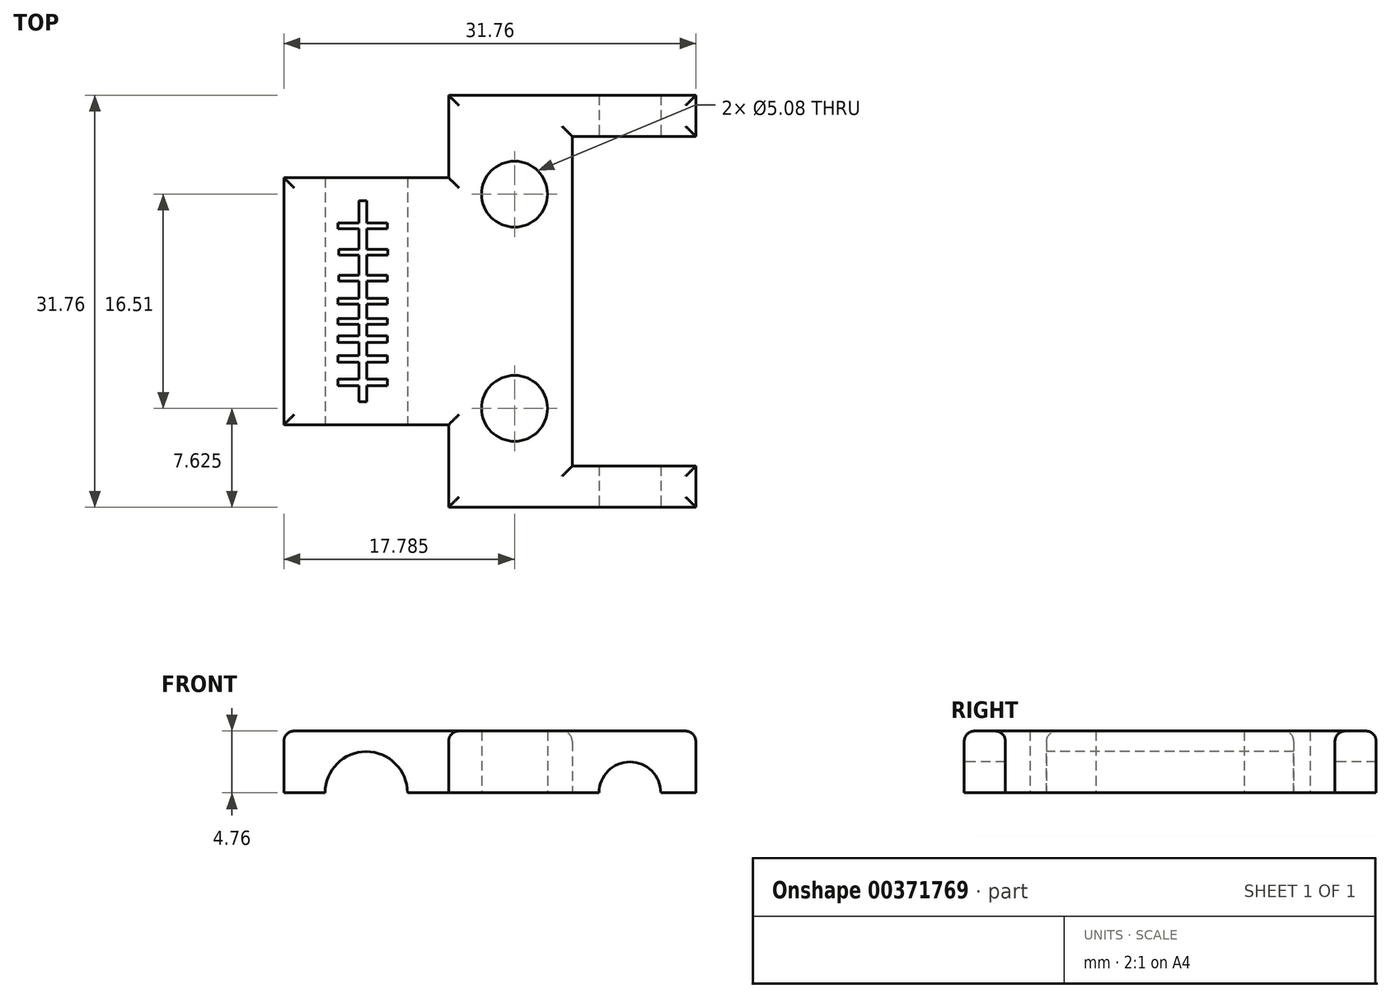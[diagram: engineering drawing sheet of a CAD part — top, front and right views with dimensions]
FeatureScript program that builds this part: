
annotation { "Feature Type Name" : "Feature", "Feature Type Description" : "" }
export const myFeature = defineFeature(function(context is Context, id is Id, definition is map)
    precondition{}
    {
        {
            var Q0;
            Q0=qCreatedBy(makeId("Top.planeOp"),FACE);
            var sketch = newSketch(context, id + "F0", { "sketchPlane" : qUnion([Q0])});
            skLineSegment(sketch, "E0.bottom", {"start": v(15.87, 15.87) * mm, "end": v(-3.18, 15.87) * mm});
            skLineSegment(sketch, "E0.top", {"start": v(15.88, -15.87) * mm, "end": v(-3.17, -15.87) * mm});
            skLineSegment(sketch, "E0.left", {"start": v(15.87, 15.88) * mm, "end": v(15.87, 12.7) * mm});
            skLineSegment(sketch, "E0.right", {"start": v(-15.88, 9.52) * mm, "end": v(-15.88, -9.52) * mm});
            skPoint(sketch, "E0.middle", {"position": v(0, 0) * mm});
            skLineSegment(sketch, "E1", {"start": v(-15.88, 9.53) * mm, "end": v(-3.17, 9.53) * mm});
            skLineSegment(sketch, "E2", {"start": v(-3.17, 9.52) * mm, "end": v(-3.18, 15.88) * mm});
            skLineSegment(sketch, "E3", {"start": v(-15.88, -9.52) * mm, "end": v(-3.17, -9.52) * mm});
            skLineSegment(sketch, "E4", {"start": v(-3.17, -9.52) * mm, "end": v(-3.17, -15.87) * mm});
            skLineSegment(sketch, "E5.trimOffspring", {"start": v(15.88, -12.7) * mm, "end": v(15.88, -15.87) * mm});
            skPoint(sketch, "E6.orphan", {"position": v(-15.88, 15.87) * mm});
            skPoint(sketch, "E7.orphan", {"position": v(-15.87, -15.88) * mm});
            skPoint(sketch, "E8.end.orphan", {"position": v(10.58, -9.52) * mm});
            skLineSegment(sketch, "E9", {"start": v(15.87, 12.7) * mm, "end": v(6.35, 12.7) * mm});
            skLineSegment(sketch, "E10", {"start": v(6.35, 12.7) * mm, "end": v(6.35, -12.7) * mm});
            skPoint(sketch, "E10.endSnap0", {"position": v(15.88, -12.7) * mm});
            skLineSegment(sketch, "E11", {"start": v(6.35, -12.7) * mm, "end": v(15.88, -12.7) * mm});
            skPoint(sketch, "E12.orphan", {"position": v(15.88, 9.53) * mm});
            skPoint(sketch, "E13.orphan", {"position": v(15.88, -9.52) * mm});
            skCircle(sketch, "E14", {"center": v(1.9, 8.25) * mm, "radius": 2.54 * mm});
            skCircle(sketch, "E15", {"center": v(1.9, -8.25) * mm, "radius": 2.54 * mm});
            skSolve(sketch);
        }
        {
            var Q0;
            Q0 = qSketchRegion(id + "F0", true);
            extrude(context, id + "F1", {"entities" : qUnion([Q0]), "depth" : 4.76 * mm});
        }
        {
            var Q0;
            Q0=makeQuery(id+"F1.opExtrude","CAP_EDGE",EDGE,{"disambiguationData":[OSD([sQuery(id+"F0.wireOp",EDGE,"E1")])],"isStart":false});
            var Q1;
            Q1=makeQuery(id+"F1.opExtrude","CAP_EDGE",EDGE,{"disambiguationData":[OSD([sQuery(id+"F0.wireOp",EDGE,"E3")])],"isStart":false});
            var Q2;
            Q2=makeQuery(id+"F1.opExtrude","CAP_EDGE",EDGE,{"disambiguationData":[OSD([sQuery(id+"F0.wireOp",EDGE,"E0.bottom")])],"isStart":false});
            var Q3;
            Q3=makeQuery(id+"F1.opExtrude","CAP_EDGE",EDGE,{"disambiguationData":[OSD([sQuery(id+"F0.wireOp",EDGE,"E9")])],"isStart":false});
            var Q4;
            Q4=makeQuery(id+"F1.opExtrude","CAP_EDGE",EDGE,{"disambiguationData":[OSD([sQuery(id+"F0.wireOp",EDGE,"E10")])],"isStart":false});
            var Q5;
            Q5=makeQuery(id+"F1.opExtrude","CAP_EDGE",EDGE,{"disambiguationData":[OSD([sQuery(id+"F0.wireOp",EDGE,"E0.left")])],"isStart":false});
            var Q6;
            Q6=makeQuery(id+"F1.opExtrude","CAP_EDGE",EDGE,{"disambiguationData":[OSD([sQuery(id+"F0.wireOp",EDGE,"E11")])],"isStart":false});
            var Q7;
            Q7=makeQuery(id+"F1.opExtrude","CAP_EDGE",EDGE,{"disambiguationData":[OSD([sQuery(id+"F0.wireOp",EDGE,"E5.trimOffspring")])],"isStart":false});
            var Q8;
            Q8=makeQuery(id+"F1.opExtrude","CAP_EDGE",EDGE,{"disambiguationData":[OSD([sQuery(id+"F0.wireOp",EDGE,"E0.top")])],"isStart":false});
            var Q9;
            Q9=makeQuery(id+"F1.opExtrude","CAP_EDGE",EDGE,{"disambiguationData":[OSD([sQuery(id+"F0.wireOp",EDGE,"E4")])],"isStart":false});
            var Q10;
            Q10=makeQuery(id+"F1.opExtrude","CAP_EDGE",EDGE,{"disambiguationData":[OSD([sQuery(id+"F0.wireOp",EDGE,"E0.right")])],"isStart":false});
            var Q11;
            Q11=makeQuery(id+"F1.opExtrude","CAP_EDGE",EDGE,{"disambiguationData":[OSD([sQuery(id+"F0.wireOp",EDGE,"E2")])],"isStart":false});
            fillet(context, id + "F2", {"entities" : qUnion([Q0, Q1, Q2, Q3, Q4, Q5, Q6, Q7, Q8, Q9, Q10, Q11]), "radius" : 0.8 * mm, "tangentPropagation" : true, "allowEdgeOverflow" : false});
        }
        {
            var Q0;
            Q0=makeQuery(id+"F1.opExtrude","SWEPT_FACE",FACE,{"disambiguationData":[OSD([sQuery(id+"F0.wireOp",EDGE,"E3")])]});
            var sketch = newSketch(context, id + "F3", { "sketchPlane" : qUnion([Q0])});
            skArc(sketch, "E16", {"start": v(-6.35, 0) * mm, "mid": v(-9.52, 3.18) * mm, "end": v(-12.7, 0) * mm});
            skLineSegment(sketch, "E17", {"start": v(-12.7, 0) * mm, "end": v(-6.35, 0) * mm});
            skSolve(sketch);
        }
        {
            var Q0;
            Q0 = qSketchRegion(id + "F3", true);
            extrude(context, id + "F4", {"entities" : qUnion([Q0]), "operationType" : NewBodyOperationType.REMOVE, "endBound" : BoundingType.THROUGH_ALL, "oppositeDirection" : true, "depth" : 25.4 * mm});
        }
        {
            var Q0;
            Q0=makeQuery(id+"F1.opExtrude","SWEPT_FACE",FACE,{"disambiguationData":[OSD([sQuery(id+"F0.wireOp",EDGE,"E0.top")])]});
            var sketch = newSketch(context, id + "F5", { "sketchPlane" : qUnion([Q0])});
            skArc(sketch, "E18", {"start": v(13.18, 0) * mm, "mid": v(10.8, 2.38) * mm, "end": v(8.41, 0) * mm});
            skLineSegment(sketch, "E19", {"start": v(8.41, 0) * mm, "end": v(13.18, 0) * mm});
            skSolve(sketch);
        }
        {
            var Q0;
            Q0 = qSketchRegion(id + "F5", true);
            extrude(context, id + "F6", {"entities" : qUnion([Q0]), "operationType" : NewBodyOperationType.REMOVE, "endBound" : BoundingType.THROUGH_ALL, "oppositeDirection" : true, "depth" : 25.4 * mm});
        }
        {
            var Q0;
            Q0=makeQuery(id+"F1.opExtrude","CAP_FACE",FACE,{"disambiguationData":[OSD([sQuery(id+"F0.wireOp",EDGE,"E0.bottom"),sQuery(id+"F0.wireOp",EDGE,"E0.top"),sQuery(id+"F0.wireOp",EDGE,"E0.left"),sQuery(id+"F0.wireOp",EDGE,"E0.right"),sQuery(id+"F0.wireOp",EDGE,"E1"),sQuery(id+"F0.wireOp",EDGE,"E2"),sQuery(id+"F0.wireOp",EDGE,"E3"),sQuery(id+"F0.wireOp",EDGE,"E4"),sQuery(id+"F0.wireOp",EDGE,"E5.trimOffspring"),sQuery(id+"F0.wireOp",EDGE,"E9"),sQuery(id+"F0.wireOp",EDGE,"E10"),sQuery(id+"F0.wireOp",EDGE,"E11"),sQuery(id+"F0.wireOp",EDGE,"E14"),sQuery(id+"F0.wireOp",EDGE,"E15")])],"isStart":false});
            var sketch = newSketch(context, id + "F7", { "sketchPlane" : qUnion([Q0])});
            skLineSegment(sketch, "E20.bottom", {"start": v(-10.1, -7.75) * mm, "end": v(-9.49, -7.75) * mm});
            skLineSegment(sketch, "E20.top", {"start": v(-10.1, 7.75) * mm, "end": v(-9.49, 7.75) * mm});
            skLineSegment(sketch, "E20.left", {"start": v(-10.1, -7.75) * mm, "end": v(-10.1, -6.51) * mm});
            skLineSegment(sketch, "E20.right", {"start": v(-9.49, -7.75) * mm, "end": v(-9.49, -6.51) * mm});
            skPoint(sketch, "E20.middle", {"position": v(-9.8, 0) * mm});
            skLineSegment(sketch, "E21.bottom", {"start": v(-11.72, 5.58) * mm, "end": v(-10.1, 5.58) * mm});
            skLineSegment(sketch, "E21.top", {"start": v(-11.72, 6.04) * mm, "end": v(-10.1, 6.04) * mm});
            skLineSegment(sketch, "E21.left", {"start": v(-11.72, 5.58) * mm, "end": v(-11.72, 6.04) * mm});
            skLineSegment(sketch, "E21.right", {"start": v(-7.9, 5.58) * mm, "end": v(-7.9, 6.04) * mm});
            skPoint(sketch, "E21.middle", {"position": v(-9.8, 5.8) * mm});
            skLineSegment(sketch, "E22.bottom", {"start": v(-7.86, 3.54) * mm, "end": v(-9.49, 3.54) * mm});
            skLineSegment(sketch, "E22.top", {"start": v(-7.86, 4) * mm, "end": v(-9.49, 4) * mm});
            skLineSegment(sketch, "E22.left", {"start": v(-7.86, 3.54) * mm, "end": v(-7.86, 4) * mm});
            skLineSegment(sketch, "E22.right", {"start": v(-11.65, 3.54) * mm, "end": v(-11.65, 4) * mm});
            skPoint(sketch, "E22.middle", {"position": v(-9.75, 3.77) * mm});
            skLineSegment(sketch, "E23.bottom", {"start": v(-7.9, 1.55) * mm, "end": v(-9.49, 1.55) * mm});
            skLineSegment(sketch, "E23.top", {"start": v(-7.9, 2) * mm, "end": v(-9.49, 2) * mm});
            skLineSegment(sketch, "E23.left", {"start": v(-7.9, 1.55) * mm, "end": v(-7.9, 2) * mm});
            skLineSegment(sketch, "E23.right", {"start": v(-11.66, 1.55) * mm, "end": v(-11.66, 2) * mm});
            skPoint(sketch, "E23.middle", {"position": v(-9.78, 1.77) * mm});
            skLineSegment(sketch, "E24.bottom", {"start": v(-7.9, -0.23) * mm, "end": v(-9.49, -0.23) * mm});
            skLineSegment(sketch, "E24.top", {"start": v(-7.9, 0.23) * mm, "end": v(-9.49, 0.23) * mm});
            skLineSegment(sketch, "E24.left", {"start": v(-7.9, -0.23) * mm, "end": v(-7.9, 0.23) * mm});
            skLineSegment(sketch, "E24.right", {"start": v(-11.7, -0.23) * mm, "end": v(-11.7, 0.23) * mm});
            skLineSegment(sketch, "E25.bottom", {"start": v(-7.9, -1.78) * mm, "end": v(-9.49, -1.78) * mm});
            skLineSegment(sketch, "E25.top", {"start": v(-7.9, -1.32) * mm, "end": v(-9.49, -1.32) * mm});
            skLineSegment(sketch, "E25.left", {"start": v(-7.9, -1.78) * mm, "end": v(-7.9, -1.32) * mm});
            skLineSegment(sketch, "E25.right", {"start": v(-11.7, -1.78) * mm, "end": v(-11.7, -1.32) * mm});
            skPoint(sketch, "E25.middle", {"position": v(-9.8, -1.55) * mm});
            skLineSegment(sketch, "E26.bottom", {"start": v(-7.9, -3.18) * mm, "end": v(-9.49, -3.18) * mm});
            skLineSegment(sketch, "E26.top", {"start": v(-7.9, -2.67) * mm, "end": v(-9.49, -2.67) * mm});
            skLineSegment(sketch, "E26.left", {"start": v(-7.9, -3.18) * mm, "end": v(-7.9, -2.67) * mm});
            skLineSegment(sketch, "E26.right", {"start": v(-11.7, -3.18) * mm, "end": v(-11.7, -2.67) * mm});
            skPoint(sketch, "E26.middle", {"position": v(-9.8, -2.93) * mm});
            skLineSegment(sketch, "E27.bottom", {"start": v(-7.9, -4.7) * mm, "end": v(-9.49, -4.7) * mm});
            skLineSegment(sketch, "E27.top", {"start": v(-7.9, -4.2) * mm, "end": v(-9.49, -4.2) * mm});
            skLineSegment(sketch, "E27.left", {"start": v(-7.9, -4.7) * mm, "end": v(-7.9, -4.2) * mm});
            skLineSegment(sketch, "E27.right", {"start": v(-11.7, -4.7) * mm, "end": v(-11.7, -4.2) * mm});
            skPoint(sketch, "E27.middle", {"position": v(-9.8, -4.45) * mm});
            skLineSegment(sketch, "E28.bottom", {"start": v(-7.9, -6.51) * mm, "end": v(-9.49, -6.51) * mm});
            skLineSegment(sketch, "E28.top", {"start": v(-7.9, -6) * mm, "end": v(-9.49, -6) * mm});
            skLineSegment(sketch, "E28.left", {"start": v(-7.9, -6.51) * mm, "end": v(-7.9, -6) * mm});
            skLineSegment(sketch, "E28.right", {"start": v(-11.7, -6.51) * mm, "end": v(-11.7, -6) * mm});
            skPoint(sketch, "E28.middle", {"position": v(-9.8, -6.26) * mm});
            skLineSegment(sketch, "E29.trimOffspring", {"start": v(-9.49, 6.04) * mm, "end": v(-9.49, 7.75) * mm});
            skLineSegment(sketch, "E30.trimOffspring", {"start": v(-10.1, 6.04) * mm, "end": v(-10.1, 7.75) * mm});
            skLineSegment(sketch, "E31.trimOffspring", {"start": v(-9.49, 5.58) * mm, "end": v(-7.9, 5.58) * mm});
            skLineSegment(sketch, "E32.trimOffspring", {"start": v(-9.49, 6.04) * mm, "end": v(-7.9, 6.04) * mm});
            skLineSegment(sketch, "E33.trimOffspring", {"start": v(-9.49, 4) * mm, "end": v(-9.49, 5.58) * mm});
            skLineSegment(sketch, "E34.trimOffspring", {"start": v(-10.1, 4) * mm, "end": v(-10.1, 5.58) * mm});
            skLineSegment(sketch, "E35.trimOffspring", {"start": v(-10.1, 4) * mm, "end": v(-11.65, 4) * mm});
            skLineSegment(sketch, "E36.trimOffspring", {"start": v(-10.1, 3.54) * mm, "end": v(-11.65, 3.54) * mm});
            skLineSegment(sketch, "E37.trimOffspring", {"start": v(-10.1, 2) * mm, "end": v(-11.66, 2) * mm});
            skLineSegment(sketch, "E38.trimOffspring", {"start": v(-10.1, 1.55) * mm, "end": v(-11.66, 1.55) * mm});
            skLineSegment(sketch, "E39.trimOffspring", {"start": v(-9.49, 2) * mm, "end": v(-9.49, 3.54) * mm});
            skLineSegment(sketch, "E40.trimOffspring", {"start": v(-10.1, 2) * mm, "end": v(-10.1, 3.54) * mm});
            skLineSegment(sketch, "E41.trimOffspring", {"start": v(-9.49, 0.23) * mm, "end": v(-9.49, 1.55) * mm});
            skLineSegment(sketch, "E42.trimOffspring", {"start": v(-10.1, 0.23) * mm, "end": v(-11.7, 0.23) * mm});
            skLineSegment(sketch, "E43.trimOffspring", {"start": v(-10.1, 0.23) * mm, "end": v(-10.1, 1.55) * mm});
            skLineSegment(sketch, "E44.trimOffspring", {"start": v(-10.1, -0.23) * mm, "end": v(-11.7, -0.23) * mm});
            skLineSegment(sketch, "E45.trimOffspring", {"start": v(-9.49, -1.32) * mm, "end": v(-9.49, -0.23) * mm});
            skLineSegment(sketch, "E46.trimOffspring", {"start": v(-10.1, -1.32) * mm, "end": v(-11.7, -1.32) * mm});
            skLineSegment(sketch, "E47.trimOffspring", {"start": v(-10.1, -1.78) * mm, "end": v(-11.7, -1.78) * mm});
            skLineSegment(sketch, "E48.trimOffspring", {"start": v(-10.1, -1.32) * mm, "end": v(-10.1, -0.23) * mm});
            skLineSegment(sketch, "E49.trimOffspring", {"start": v(-9.49, -2.67) * mm, "end": v(-9.49, -1.78) * mm});
            skLineSegment(sketch, "E50.trimOffspring", {"start": v(-10.1, -3.18) * mm, "end": v(-11.7, -3.18) * mm});
            skLineSegment(sketch, "E51.trimOffspring", {"start": v(-10.1, -2.67) * mm, "end": v(-11.7, -2.67) * mm});
            skLineSegment(sketch, "E52.trimOffspring", {"start": v(-10.1, -2.67) * mm, "end": v(-10.1, -1.78) * mm});
            skLineSegment(sketch, "E53.trimOffspring", {"start": v(-9.49, -6) * mm, "end": v(-9.49, -4.7) * mm});
            skLineSegment(sketch, "E54.trimOffspring", {"start": v(-10.1, -6) * mm, "end": v(-10.1, -4.7) * mm});
            skLineSegment(sketch, "E55.trimOffspring", {"start": v(-10.1, -6) * mm, "end": v(-11.7, -6) * mm});
            skLineSegment(sketch, "E56.trimOffspring", {"start": v(-10.1, -6.51) * mm, "end": v(-11.7, -6.51) * mm});
            skLineSegment(sketch, "E57.trimOffspring", {"start": v(-10.1, -4.7) * mm, "end": v(-11.7, -4.7) * mm});
            skLineSegment(sketch, "E58.trimOffspring", {"start": v(-9.49, -4.2) * mm, "end": v(-9.49, -3.18) * mm});
            skLineSegment(sketch, "E59.trimOffspring", {"start": v(-10.1, -4.2) * mm, "end": v(-11.7, -4.2) * mm});
            skLineSegment(sketch, "E60.trimOffspring", {"start": v(-10.1, -4.2) * mm, "end": v(-10.1, -3.18) * mm});
            skSolve(sketch);
        }
        {
            var Q0;
            Q0 = qSketchRegion(id + "F7", true);
            extrude(context, id + "F8", {"entities" : qUnion([Q0]), "operationType" : NewBodyOperationType.REMOVE, "oppositeDirection" : true, "depth" : 0.03 * mm});
        }
    });
